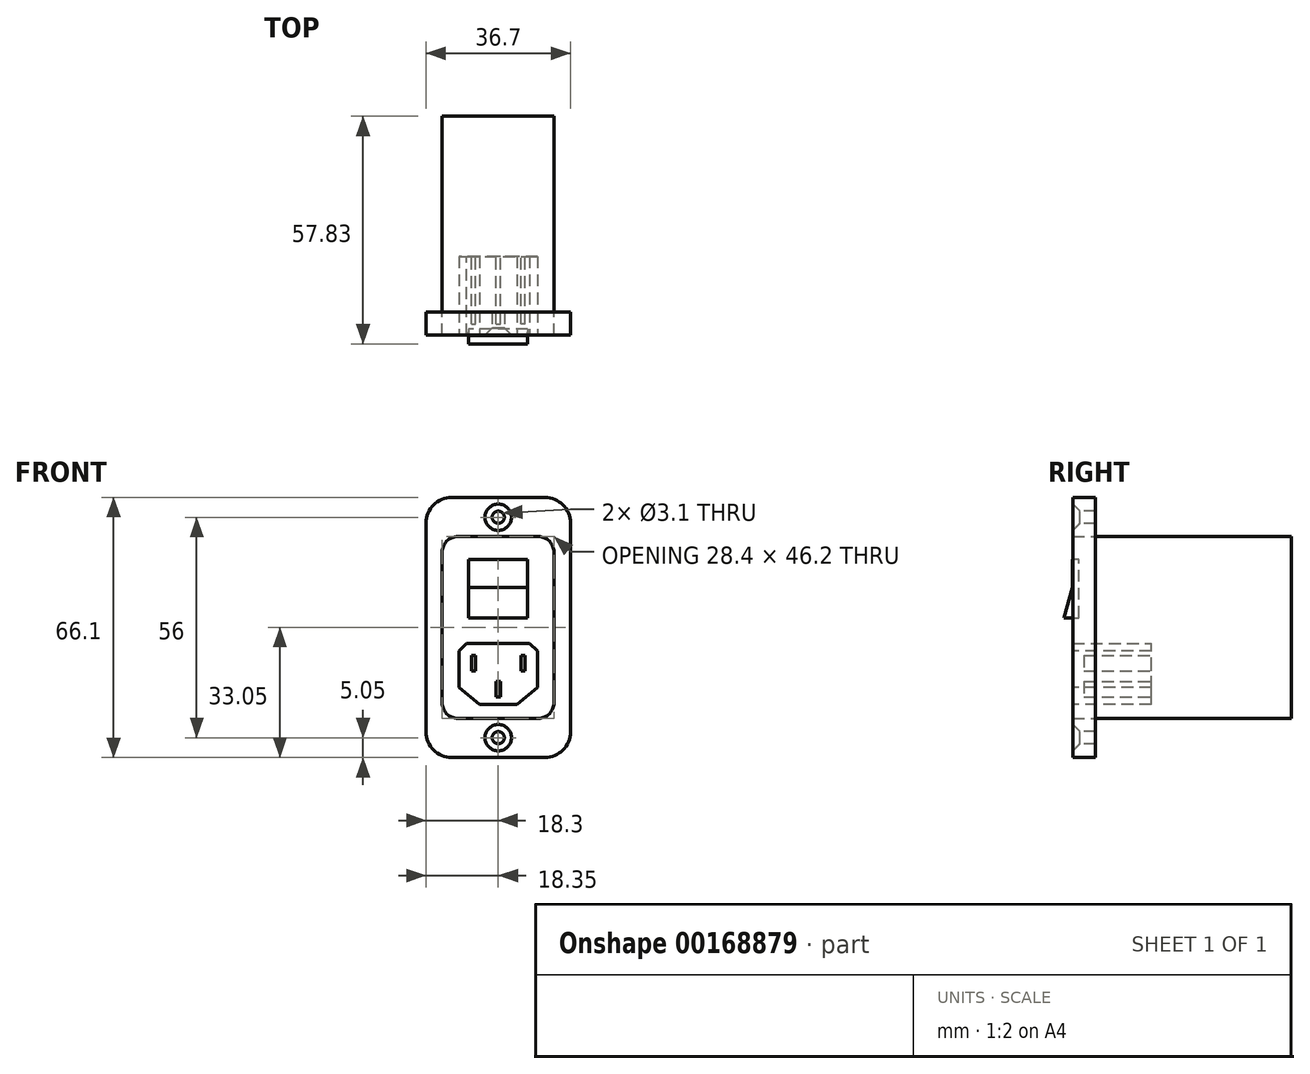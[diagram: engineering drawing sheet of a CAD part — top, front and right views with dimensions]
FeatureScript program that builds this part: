
annotation { "Feature Type Name" : "Feature", "Feature Type Description" : "" }
export const myFeature = defineFeature(function(context is Context, id is Id, definition is map)
    precondition{}
    {
        {
            var Q0;
            Q0=qCreatedBy(makeId("Front.planeOp"),FACE);
            var sketch = newSketch(context, id + "F0", { "sketchPlane" : qUnion([Q0])});
            skLineSegment(sketch, "E0.bottom", {"start": v(-10.25, 23.1) * mm, "end": v(10.15, 23.1) * mm});
            skLineSegment(sketch, "E0.top", {"start": v(-10.25, -23.1) * mm, "end": v(10.15, -23.1) * mm});
            skLineSegment(sketch, "E0.left", {"start": v(-14.25, 19.1) * mm, "end": v(-14.25, -19.1) * mm});
            skLineSegment(sketch, "E0.right", {"start": v(14.15, 19.1) * mm, "end": v(14.15, -19.1) * mm});
            skLineSegment(sketch, "E1", {"start": v(-100.57, 0) * mm, "end": v(-8.57, 0) * mm, "construction": true});
            skPoint(sketch, "E2.visualSharp", {"position": v(14.15, 23.1) * mm});
            skArc(sketch, "E2.filletArc", {"start": v(14.15, 19.1) * mm, "mid": v(12.98, 21.93) * mm, "end": v(10.15, 23.1) * mm});
            skPoint(sketch, "E3.visualSharp", {"position": v(-14.25, 23.1) * mm});
            skArc(sketch, "E3.filletArc", {"start": v(-10.25, 23.1) * mm, "mid": v(-13.08, 21.93) * mm, "end": v(-14.25, 19.1) * mm});
            skPoint(sketch, "E4.visualSharp", {"position": v(-14.25, -23.1) * mm});
            skArc(sketch, "E4.filletArc", {"start": v(-14.25, -19.1) * mm, "mid": v(-13.08, -21.93) * mm, "end": v(-10.25, -23.1) * mm});
            skPoint(sketch, "E5.visualSharp", {"position": v(14.15, -23.1) * mm});
            skArc(sketch, "E5.filletArc", {"start": v(10.15, -23.1) * mm, "mid": v(12.98, -21.93) * mm, "end": v(14.15, -19.1) * mm});
            skLineSegment(sketch, "E6.bottom", {"start": v(11.85, -33.05) * mm, "end": v(-11.85, -33.05) * mm});
            skLineSegment(sketch, "E6.top", {"start": v(11.85, 33.05) * mm, "end": v(-11.85, 33.05) * mm});
            skLineSegment(sketch, "E6.left", {"start": v(18.35, -26.55) * mm, "end": v(18.35, 26.55) * mm});
            skLineSegment(sketch, "E6.right", {"start": v(-18.35, -26.55) * mm, "end": v(-18.35, 26.55) * mm});
            skPoint(sketch, "E6.middle", {"position": v(0, 0) * mm});
            skPoint(sketch, "E7.visualSharp", {"position": v(-18.35, 33.05) * mm});
            skArc(sketch, "E7.filletArc", {"start": v(-11.85, 33.05) * mm, "mid": v(-16.45, 31.15) * mm, "end": v(-18.35, 26.55) * mm});
            skPoint(sketch, "E8.visualSharp", {"position": v(18.35, 33.05) * mm});
            skArc(sketch, "E8.filletArc", {"start": v(18.35, 26.55) * mm, "mid": v(16.45, 31.15) * mm, "end": v(11.85, 33.05) * mm});
            skPoint(sketch, "E9.visualSharp", {"position": v(18.35, -33.05) * mm});
            skArc(sketch, "E9.filletArc", {"start": v(11.85, -33.05) * mm, "mid": v(16.45, -31.15) * mm, "end": v(18.35, -26.55) * mm});
            skPoint(sketch, "E10.visualSharp", {"position": v(-18.35, -33.05) * mm});
            skArc(sketch, "E10.filletArc", {"start": v(-18.35, -26.55) * mm, "mid": v(-16.45, -31.15) * mm, "end": v(-11.85, -33.05) * mm});
            skSolve(sketch);
        }
        {
            var Q0;
            Q0=qSketchRegion(id+"F0",true);
            extrude(context, id + "F1", {"entities" : qUnion([Q0]), "depth" : 5.8 * mm});
        }
        {
            var Q0;
            Q0=makeQuery(id+"F0.imprint","IMPRINT",FACE,{"disambiguationData":[TD([[makeQuery(id+"F0.imprint","IMPRINT",EDGE,{"derivedFrom":sQuery(id+"F0.wireOp",EDGE,"E0.bottom")}),-1.0]])]});
            extrude(context, id + "F2", {"entities" : qUnion([Q0]), "depth" : 5.8 * mm, "hasSecondDirection" : true, "secondDirectionOppositeDirection" : true, "secondDirectionDepth" : 49.8 * mm});
        }
        {
            var Q0;
            Q0=makeQuery(id+"F1.opExtrude","CAP_FACE",FACE,{"disambiguationData":[OSD([sQuery(id+"F0.wireOp",EDGE,"E0.bottom"),sQuery(id+"F0.wireOp",EDGE,"E0.top"),sQuery(id+"F0.wireOp",EDGE,"E0.left"),sQuery(id+"F0.wireOp",EDGE,"E0.right"),sQuery(id+"F0.wireOp",EDGE,"E2.filletArc"),sQuery(id+"F0.wireOp",EDGE,"E3.filletArc"),sQuery(id+"F0.wireOp",EDGE,"E4.filletArc"),sQuery(id+"F0.wireOp",EDGE,"E5.filletArc"),sQuery(id+"F0.wireOp",EDGE,"E6.bottom"),sQuery(id+"F0.wireOp",EDGE,"E6.top"),sQuery(id+"F0.wireOp",EDGE,"E6.left"),sQuery(id+"F0.wireOp",EDGE,"E6.right"),sQuery(id+"F0.wireOp",EDGE,"E7.filletArc"),sQuery(id+"F0.wireOp",EDGE,"E8.filletArc"),sQuery(id+"F0.wireOp",EDGE,"E9.filletArc"),sQuery(id+"F0.wireOp",EDGE,"E10.filletArc")])],"isStart":false});
            var sketch = newSketch(context, id + "F3", { "sketchPlane" : qUnion([Q0])});
            skLineSegment(sketch, "E11", {"start": v(-9.4, 28) * mm, "end": v(9.42, 28) * mm, "construction": true});
            skLineSegment(sketch, "E12.MirrorCS", {"start": v(-9.4, -28) * mm, "end": v(9.42, -28) * mm, "construction": true});
            skLineSegment(sketch, "E13", {"start": v(0, 31.17) * mm, "end": v(0, -30.42) * mm, "construction": true});
            skPoint(sketch, "E14", {"position": v(0, -28) * mm});
            skPoint(sketch, "E15", {"position": v(0, 28) * mm});
            skSolve(sketch);
        }
        {
            var Q0;
            Q0=sQuery(id+"F3.wireOp",VERTEX,"E15");
            var Q1;
            Q1=sQuery(id+"F3.wireOp",VERTEX,"E14");
            var Q2;
            Q2=makeQuery(id+"F1.opExtrude","SWEPT_BODY",BODY,{"disambiguationData":[OSD([sQuery(id+"F0.wireOp",EDGE,"E0.bottom"),sQuery(id+"F0.wireOp",EDGE,"E0.top"),sQuery(id+"F0.wireOp",EDGE,"E0.left"),sQuery(id+"F0.wireOp",EDGE,"E0.right"),sQuery(id+"F0.wireOp",EDGE,"E2.filletArc"),sQuery(id+"F0.wireOp",EDGE,"E3.filletArc"),sQuery(id+"F0.wireOp",EDGE,"E4.filletArc"),sQuery(id+"F0.wireOp",EDGE,"E5.filletArc"),sQuery(id+"F0.wireOp",EDGE,"E6.bottom"),sQuery(id+"F0.wireOp",EDGE,"E6.top"),sQuery(id+"F0.wireOp",EDGE,"E6.left"),sQuery(id+"F0.wireOp",EDGE,"E6.right"),sQuery(id+"F0.wireOp",EDGE,"E7.filletArc"),sQuery(id+"F0.wireOp",EDGE,"E8.filletArc"),sQuery(id+"F0.wireOp",EDGE,"E9.filletArc"),sQuery(id+"F0.wireOp",EDGE,"E10.filletArc")])]});
            hole(context, id + "F4", {"style" : HoleStyle.C_SINK, "endStyle" : HoleEndStyle.THROUGH, "holeDiameter" : 3.1 * mm, "cSinkDiameter" : 6.72 * mm, "cSinkAngle" : 90 * degree, "startFromSketch" : true, "locations" : qUnion([Q0, Q1]), "scope" : qUnion([Q2]), "isTappedThrough" : true});
        }
        {
            var Q0;
            Q0=makeQuery(id+"F2.opExtrude","CAP_FACE",FACE,{"disambiguationData":[OSD([sQuery(id+"F0.wireOp",EDGE,"E0.bottom"),sQuery(id+"F0.wireOp",EDGE,"E0.top"),sQuery(id+"F0.wireOp",EDGE,"E0.left"),sQuery(id+"F0.wireOp",EDGE,"E0.right"),sQuery(id+"F0.wireOp",EDGE,"E2.filletArc"),sQuery(id+"F0.wireOp",EDGE,"E3.filletArc"),sQuery(id+"F0.wireOp",EDGE,"E4.filletArc"),sQuery(id+"F0.wireOp",EDGE,"E5.filletArc")])],"isStart":false});
            var sketch = newSketch(context, id + "F5", { "sketchPlane" : qUnion([Q0])});
            skLineSegment(sketch, "E16", {"start": v(-10, -4) * mm, "end": v(10, -4) * mm});
            skLineSegment(sketch, "E17", {"start": v(10, -4) * mm, "end": v(10, -15.28) * mm});
            skLineSegment(sketch, "E18", {"start": v(10, -15.28) * mm, "end": v(4.75, -19.5) * mm});
            skLineSegment(sketch, "E19", {"start": v(4.75, -19.5) * mm, "end": v(-4.75, -19.5) * mm});
            skLineSegment(sketch, "E20", {"start": v(-4.75, -19.5) * mm, "end": v(-10, -15.28) * mm});
            skLineSegment(sketch, "E21", {"start": v(-10, -15.28) * mm, "end": v(-10, -4) * mm});
            skSolve(sketch);
        }
        {
            var Q0;
            Q0=makeQuery(id+"F5.imprint","IMPRINT",FACE,{"disambiguationData":[TD([[makeQuery(id+"F5.imprint","IMPRINT",EDGE,{"derivedFrom":sQuery(id+"F5.wireOp",EDGE,"E16")}),-1.0]])]});
            extrude(context, id + "F6", {"entities" : qUnion([Q0]), "operationType" : NewBodyOperationType.REMOVE, "oppositeDirection" : true, "depth" : 20 * mm});
        }
        {
            var Q0;
            Q0=makeQuery(id+"F6.boolean.opBoolean","COPY",EDGE,{"derivedFrom":makeQuery(id+"F6.opExtrude","SWEPT_EDGE",EDGE,{"disambiguationData":[OSD([sQuery(id+"F5.wireOp",EDGE,"E16"),sQuery(id+"F5.wireOp",EDGE,"E17")])]})});
            var Q1;
            Q1=makeQuery(id+"F6.boolean.opBoolean","COPY",EDGE,{"derivedFrom":makeQuery(id+"F6.opExtrude","SWEPT_EDGE",EDGE,{"disambiguationData":[OSD([sQuery(id+"F5.wireOp",EDGE,"E16"),sQuery(id+"F5.wireOp",EDGE,"E21")])]})});
            chamfer(context, id + "F7", {"entities" : qUnion([Q0, Q1]), "width" : 2 * mm, "tangentPropagation" : true});
        }
        {
            var Q0;
            Q0=makeQuery(id+"F0.imprint","IMPRINT",FACE,{"disambiguationData":[TD([[makeQuery(id+"F0.imprint","IMPRINT",EDGE,{"derivedFrom":sQuery(id+"F0.wireOp",EDGE,"E0.bottom")}),-1.0]])]});
            var sketch = newSketch(context, id + "F8", { "sketchPlane" : qUnion([Q0])});
            skLineSegment(sketch, "E22.bottom", {"start": v(-6.84, -7.13) * mm, "end": v(-5.74, -7.13) * mm});
            skLineSegment(sketch, "E22.top", {"start": v(-6.84, -11.08) * mm, "end": v(-5.74, -11.08) * mm});
            skLineSegment(sketch, "E22.left", {"start": v(-6.84, -7.13) * mm, "end": v(-6.84, -11.08) * mm});
            skLineSegment(sketch, "E22.right", {"start": v(-5.74, -7.13) * mm, "end": v(-5.74, -11.08) * mm});
            skLineSegment(sketch, "E23.MirrorCS", {"start": v(6.84, -7.13) * mm, "end": v(6.84, -11.08) * mm});
            skLineSegment(sketch, "E24.MirrorCS", {"start": v(5.74, -7.13) * mm, "end": v(5.74, -11.08) * mm});
            skLineSegment(sketch, "E25.MirrorCS", {"start": v(6.84, -7.13) * mm, "end": v(5.74, -7.13) * mm});
            skLineSegment(sketch, "E26.MirrorCS", {"start": v(6.84, -11.08) * mm, "end": v(5.74, -11.08) * mm});
            skLineSegment(sketch, "E27.1.0.0", {"start": v(-0.58, -13.73) * mm, "end": v(0.53, -13.73) * mm});
            skLineSegment(sketch, "E27.1.0.1", {"start": v(0.53, -13.73) * mm, "end": v(0.53, -17.68) * mm});
            skLineSegment(sketch, "E27.1.0.2", {"start": v(-0.58, -13.73) * mm, "end": v(-0.58, -17.68) * mm});
            skLineSegment(sketch, "E27.1.0.3", {"start": v(-0.58, -17.68) * mm, "end": v(0.53, -17.68) * mm});
            skLineSegment(sketch, "E27.direction1", {"start": v(-6.84, -7.13) * mm, "end": v(-0.58, -13.73) * mm, "construction": true});
            skSolve(sketch);
        }
        {
            var Q0;
            Q0=qSketchRegion(id+"F8",true);
            extrude(context, id + "F9", {"entities" : qUnion([Q0]), "operationType" : NewBodyOperationType.ADD, "depth" : 3 * mm, "hasSecondDirection" : true, "secondDirectionOppositeDirection" : true, "secondDirectionDepth" : 15 * mm});
        }
        {
            var Q0;
            Q0=qCreatedBy(makeId("Right.planeOp"),FACE);
            var sketch = newSketch(context, id + "F10", { "sketchPlane" : qUnion([Q0])});
            skLineSegment(sketch, "E28", {"start": v(-5.8, 22.98) * mm, "end": v(-5.8, -9.29) * mm, "construction": true});
            skLineSegment(sketch, "E29", {"start": v(-5.8, 17.32) * mm, "end": v(-5.8, 10.18) * mm});
            skLineSegment(sketch, "E30", {"start": v(-5.91, 10.18) * mm, "end": v(-8.03, 2.47) * mm});
            skLineSegment(sketch, "E31", {"start": v(-8.03, 2.47) * mm, "end": v(-4.29, 2.47) * mm});
            skLineSegment(sketch, "E32", {"start": v(-4.29, 2.47) * mm, "end": v(-4.29, 17.32) * mm});
            skLineSegment(sketch, "E33", {"start": v(-4.29, 17.32) * mm, "end": v(-5.91, 17.32) * mm});
            skLineSegment(sketch, "E34", {"start": v(-5.91, 17.32) * mm, "end": v(-5.91, 10.18) * mm});
            skSolve(sketch);
        }
        {
            var Q0;
            Q0=qSketchRegion(id+"F10",true);
            extrude(context, id + "F11", {"entities" : qUnion([Q0]), "endBound" : BoundingType.SYMMETRIC, "depth" : 15 * mm});
        }
    });
